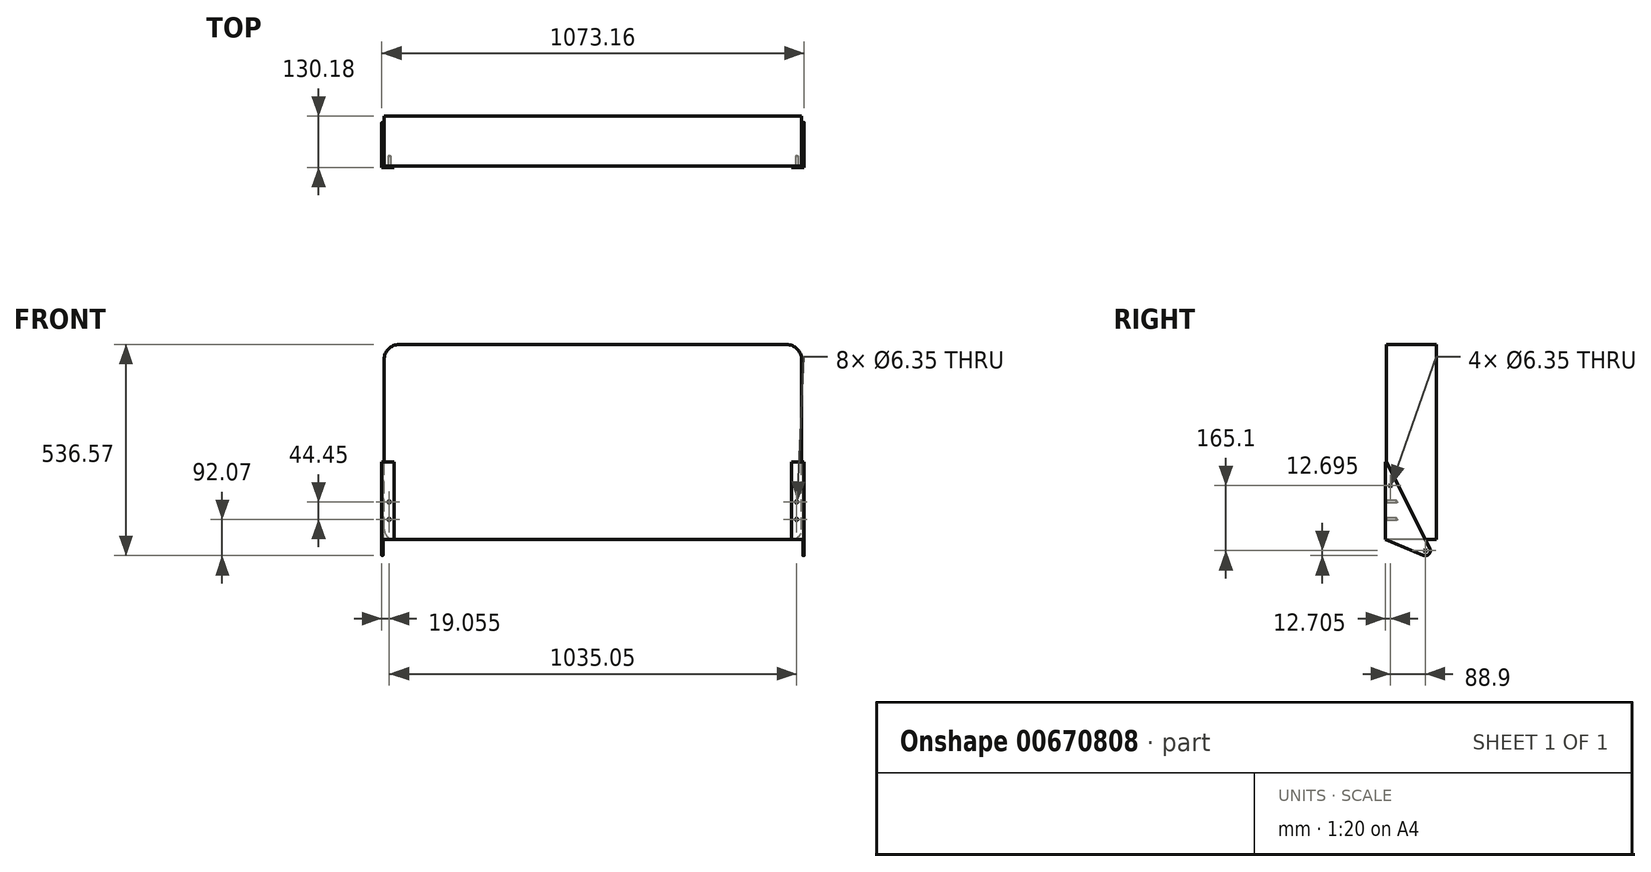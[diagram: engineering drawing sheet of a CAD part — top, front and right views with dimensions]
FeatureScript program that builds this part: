
annotation { "Feature Type Name" : "Feature", "Feature Type Description" : "" }
export const myFeature = defineFeature(function(context is Context, id is Id, definition is map)
    precondition{}
    {
        {
            var Q0;
            Q0=qCreatedBy(makeId("Front.planeOp"),FACE);
            var sketch = newSketch(context, id + "F0", { "sketchPlane" : qUnion([Q0])});
            skLineSegment(sketch, "E0.bottom", {"start": v(504.83, 0) * mm, "end": v(-504.83, 0) * mm});
            skLineSegment(sketch, "E0.top", {"start": v(492.13, 495.3) * mm, "end": v(-492.13, 495.3) * mm});
            skLineSegment(sketch, "E0.left", {"start": v(530.23, 25.4) * mm, "end": v(530.23, 457.2) * mm});
            skLineSegment(sketch, "E0.right", {"start": v(-530.23, 25.4) * mm, "end": v(-530.23, 457.2) * mm});
            skPoint(sketch, "E1.visualSharp", {"position": v(530.23, 495.3) * mm});
            skArc(sketch, "E1.filletArc", {"start": v(530.23, 457.2) * mm, "mid": v(519.07, 484.14) * mm, "end": v(492.13, 495.3) * mm});
            skPoint(sketch, "E2.visualSharp", {"position": v(-530.23, 495.3) * mm});
            skArc(sketch, "E2.filletArc", {"start": v(-492.13, 495.3) * mm, "mid": v(-519.07, 484.14) * mm, "end": v(-530.23, 457.2) * mm});
            skPoint(sketch, "E3.visualSharp", {"position": v(530.23, 0) * mm});
            skArc(sketch, "E3.filletArc", {"start": v(504.83, 0) * mm, "mid": v(522.79, 7.44) * mm, "end": v(530.23, 25.4) * mm});
            skPoint(sketch, "E4.visualSharp", {"position": v(-530.23, 0) * mm});
            skArc(sketch, "E4.filletArc", {"start": v(-530.22, 25.4) * mm, "mid": v(-522.79, 7.44) * mm, "end": v(-504.83, 0) * mm});
            skLineSegment(sketch, "E5", {"start": v(530.23, 241.3) * mm, "end": v(415.93, 241.3) * mm, "construction": true});
            skLineSegment(sketch, "E6", {"start": v(415.93, 241.3) * mm, "end": v(117.48, 241.3) * mm, "construction": true});
            skLineSegment(sketch, "E7", {"start": v(117.48, 241.3) * mm, "end": v(-104.77, 241.3) * mm, "construction": true});
            skLineSegment(sketch, "E8", {"start": v(-104.77, 241.3) * mm, "end": v(-403.22, 241.3) * mm, "construction": true});
            skLineSegment(sketch, "E9", {"start": v(-403.22, 241.3) * mm, "end": v(-530.23, 241.3) * mm, "construction": true});
            skLineSegment(sketch, "E10", {"start": v(415.93, 0) * mm, "end": v(415.93, 495.3) * mm});
            skLineSegment(sketch, "E11", {"start": v(117.48, 0) * mm, "end": v(117.48, 495.3) * mm});
            skLineSegment(sketch, "E12", {"start": v(-104.77, 0) * mm, "end": v(-104.77, 495.3) * mm});
            skLineSegment(sketch, "E13", {"start": v(-403.22, 0) * mm, "end": v(-403.22, 495.3) * mm});
            skLineSegment(sketch, "E14", {"start": v(-517.52, 0) * mm, "end": v(-517.52, 50.8) * mm, "construction": true});
            skLineSegment(sketch, "E15", {"start": v(-517.52, 50.8) * mm, "end": v(-530.22, 50.8) * mm, "construction": true});
            skLineSegment(sketch, "E16", {"start": v(-517.52, 50.8) * mm, "end": v(-517.52, 95.25) * mm, "construction": true});
            skLineSegment(sketch, "E17.MirrorCS", {"start": v(517.52, 50.8) * mm, "end": v(517.52, 95.25) * mm, "construction": true});
            skLineSegment(sketch, "E18.MirrorCS", {"start": v(517.52, 50.8) * mm, "end": v(530.22, 50.8) * mm, "construction": true});
            skLineSegment(sketch, "E19.MirrorCS", {"start": v(517.52, 0) * mm, "end": v(517.52, 50.8) * mm, "construction": true});
            skSolve(sketch);
        }
        {
            var Q0;
            Q0=makeQuery(id+"F0.imprint","IMPRINT",FACE,{"disambiguationData":[TD([[makeQuery(id+"F0.imprint","IMPRINT",EDGE,{"derivedFrom":sQuery(id+"F0.wireOp",EDGE,"E0.left")}),1.0]])]});
            var Q1;
            {var subQ0=sQuery(id+"F0.wireOp",EDGE,"E10");Q1=makeQuery(id+"F0.imprint","IMPRINT",FACE,{"disambiguationData":[TD([[makeQuery(id+"F0.imprint","IMPRINT",EDGE,{"derivedFrom":subQ0}),1.0]])]});}
            var Q2;
            {var subQ0=sQuery(id+"F0.wireOp",EDGE,"E11");Q2=makeQuery(id+"F0.imprint","IMPRINT",FACE,{"disambiguationData":[TD([[makeQuery(id+"F0.imprint","IMPRINT",EDGE,{"derivedFrom":subQ0}),1.0]])]});}
            var Q3;
            {var subQ0=sQuery(id+"F0.wireOp",EDGE,"E12");Q3=makeQuery(id+"F0.imprint","IMPRINT",FACE,{"disambiguationData":[TD([[makeQuery(id+"F0.imprint","IMPRINT",EDGE,{"derivedFrom":subQ0}),1.0]])]});}
            var Q4;
            Q4=makeQuery(id+"F0.imprint","IMPRINT",FACE,{"disambiguationData":[TD([[makeQuery(id+"F0.imprint","IMPRINT",EDGE,{"derivedFrom":sQuery(id+"F0.wireOp",EDGE,"E0.right")}),-1.0]])]});
            extrude(context, id + "F1", {"entities" : qUnion([Q0, Q1, Q2, Q3, Q4]), "oppositeDirection" : true, "depth" : 127 * mm, "offsetDistance" : 25.4 * mm});
        }
        {
            var Q0;
            Q0=sQuery(id+"F0.wireOp",VERTEX,"E16.end");
            var Q1;
            Q1=sQuery(id+"F0.wireOp",VERTEX,"E16.start");
            var Q2;
            Q2=sQuery(id+"F0.wireOp",VERTEX,"E17.MirrorCS.end");
            var Q3;
            Q3=sQuery(id+"F0.wireOp",VERTEX,"E19.MirrorCS.end");
            var Q4;
            Q4=makeQuery(id+"F1.opExtrude","SWEPT_BODY",BODY,{"disambiguationData":[OSD([sQuery(id+"F0.wireOp",EDGE,"E0.bottom"),sQuery(id+"F0.wireOp",EDGE,"E0.top"),sQuery(id+"F0.wireOp",EDGE,"E0.left"),sQuery(id+"F0.wireOp",EDGE,"E0.right"),sQuery(id+"F0.wireOp",EDGE,"E1.filletArc"),sQuery(id+"F0.wireOp",EDGE,"E2.filletArc"),sQuery(id+"F0.wireOp",EDGE,"E3.filletArc"),sQuery(id+"F0.wireOp",EDGE,"E4.filletArc")])]});
            hole(context, id + "F2", {"style" : HoleStyle.SIMPLE, "endStyle" : HoleEndStyle.BLIND, "holeDiameter" : 6.35 * mm, "majorDiameter" : 6.35 * mm, "holeDepth" : 25.4 * mm, "isTappedThrough" : true, "tappedDepth" : 12.7 * mm, "tapClearance" : 3, "locations" : qUnion([Q0, Q1, Q2, Q3]), "scope" : qUnion([Q4])});
        }
        {
            var Q0;
            Q0=makeQuery(id+"F0.imprint","IMPRINT",FACE,{"disambiguationData":[TD([[makeQuery(id+"F0.imprint","IMPRINT",EDGE,{"derivedFrom":sQuery(id+"F0.wireOp",EDGE,"E0.left")}),1.0]])]});
            var sketch = newSketch(context, id + "F3", { "sketchPlane" : qUnion([Q0])});
            skLineSegment(sketch, "E20.0", {"start": v(517.52, 50.8) * mm, "end": v(517.52, 95.25) * mm, "construction": true});
            skLineSegment(sketch, "E20.1", {"start": v(517.52, 0) * mm, "end": v(517.52, 50.8) * mm, "construction": true});
            skLineSegment(sketch, "E21.0", {"start": v(498.48, 0) * mm, "end": v(-504.83, 0) * mm, "construction": true});
            skLineSegment(sketch, "E22.0", {"start": v(530.23, 25.4) * mm, "end": v(530.23, 457.2) * mm, "construction": true});
            skLineSegment(sketch, "E23.bottom", {"start": v(504.82, 196.85) * mm, "end": v(536.58, 196.85) * mm});
            skLineSegment(sketch, "E23.top", {"start": v(504.82, 0) * mm, "end": v(536.58, 0) * mm});
            skLineSegment(sketch, "E23.left", {"start": v(504.82, 196.85) * mm, "end": v(504.82, 0) * mm});
            skLineSegment(sketch, "E23.right", {"start": v(536.58, 196.85) * mm, "end": v(536.58, 0) * mm});
            skLineSegment(sketch, "E24", {"start": v(517.52, 95.25) * mm, "end": v(517.52, 196.85) * mm, "construction": true});
            skLineSegment(sketch, "E25", {"start": v(517.52, 95.25) * mm, "end": v(504.82, 95.25) * mm, "construction": true});
            skLineSegment(sketch, "E26", {"start": v(530.23, 95.25) * mm, "end": v(536.58, 95.25) * mm, "construction": true});
            skArc(sketch, "E27.0", {"start": v(504.83, 0) * mm, "mid": v(522.79, 7.44) * mm, "end": v(530.23, 25.4) * mm, "construction": true});
            skSolve(sketch);
        }
        {
            var Q0;
            {var subQ0=sQuery(id+"F3.wireOp",EDGE,"E23.left");Q0=makeQuery(id+"F3.imprint","IMPRINT",FACE,{"disambiguationData":[TD([[makeQuery(id+"F3.imprint","IMPRINT",EDGE,{"derivedFrom":subQ0}),1.0]])]});}
            var Q1;
            Q1=makeQuery(id+"F3.imprint","IMPRINT",FACE,{"disambiguationData":[TD([[makeQuery(id+"F3.imprint","IMPRINT",EDGE,{"derivedFrom":sQuery(id+"F3.wireOp",EDGE,"E23.top")}),1.0]])]});
            extrude(context, id + "F4", {"entities" : qUnion([Q0, Q1]), "depth" : 3.17 * mm, "offsetDistance" : 25.4 * mm});
        }
        {
            var Q0;
            Q0=sQuery(id+"F0.wireOp",VERTEX,"E17.MirrorCS.end");
            var Q1;
            Q1=sQuery(id+"F0.wireOp",VERTEX,"E17.MirrorCS.start");
            var Q2;
            Q2=makeQuery(id+"F4.opExtrude","SWEPT_BODY",BODY,{"disambiguationData":[OSD([sQuery(id+"F3.wireOp",EDGE,"E23.bottom"),sQuery(id+"F3.wireOp",EDGE,"E23.top"),sQuery(id+"F3.wireOp",EDGE,"E23.left"),sQuery(id+"F3.wireOp",EDGE,"E23.right")])]});
            hole(context, id + "F5", {"style" : HoleStyle.SIMPLE, "endStyle" : HoleEndStyle.THROUGH, "oppositeDirection" : true, "holeDiameter" : 6.35 * mm, "majorDiameter" : 6.35 * mm, "isTappedThrough" : true, "tappedDepth" : 12.7 * mm, "tapClearance" : 3, "locations" : qUnion([Q0, Q1]), "scope" : qUnion([Q2])});
        }
        {
            var Q0;
            Q0=makeQuery(id+"F4.opExtrude","SWEPT_FACE",FACE,{"disambiguationData":[OSD([sQuery(id+"F3.wireOp",EDGE,"E23.right")])]});
            var sketch = newSketch(context, id + "F6", { "sketchPlane" : qUnion([Q0])});
            skLineSegment(sketch, "E28.0", {"start": v(0, 50.8) * mm, "end": v(0, 95.25) * mm, "construction": true});
            skLineSegment(sketch, "E29", {"start": v(0, 50.8) * mm, "end": v(0, -28.58) * mm, "construction": true});
            skLineSegment(sketch, "E30", {"start": v(0, -28.58) * mm, "end": v(98.43, -28.58) * mm, "construction": true});
            skArc(sketch, "E31", {"start": v(93.54, -40.3) * mm, "mid": v(107.7, -37.24) * mm, "end": v(109.79, -22.9) * mm});
            skLineSegment(sketch, "E32", {"start": v(0, 196.85) * mm, "end": v(109.79, -22.9) * mm});
            skLineSegment(sketch, "E33.0", {"start": v(-3.18, 196.85) * mm, "end": v(-3.18, 0) * mm});
            skLineSegment(sketch, "E34.0", {"start": v(-3.18, 196.85) * mm, "end": v(0, 196.85) * mm});
            skLineSegment(sketch, "E35", {"start": v(-3.17, 0) * mm, "end": v(93.54, -40.3) * mm});
            skLineSegment(sketch, "E36", {"start": v(98.43, -28.58) * mm, "end": v(98.43, 136.52) * mm, "construction": true});
            skLineSegment(sketch, "E37", {"start": v(98.43, 136.52) * mm, "end": v(9.53, 136.52) * mm, "construction": true});
            skSolve(sketch);
        }
        {
            var Q0;
            Q0=makeQuery(id+"F6.imprint","IMPRINT",FACE,{"disambiguationData":[TD([[makeQuery(id+"F6.imprint","IMPRINT",EDGE,{"derivedFrom":sQuery(id+"F6.wireOp",EDGE,"E31")}),1.0]])]});
            var Q1;
            Q1=makeQuery(id+"F6.imprint","IMPRINT",FACE,{"disambiguationData":[TD([[makeQuery(id+"F6.imprint","IMPRINT",EDGE,{"derivedFrom":sQuery(id+"F6.wireOp",EDGE,"E33.0")}),1.0]])]});
            extrude(context, id + "F7", {"entities" : qUnion([Q0, Q1]), "operationType" : NewBodyOperationType.ADD, "oppositeDirection" : true, "depth" : 3.17 * mm, "offsetDistance" : 25.4 * mm});
        }
        {
            var Q0;
            Q0=sQuery(id+"F6.wireOp",VERTEX,"E30.end");
            var Q1;
            Q1=sQuery(id+"F6.wireOp",VERTEX,"E37.end");
            var Q2;
            Q2=makeQuery(id+"F4.opExtrude","SWEPT_BODY",BODY,{"disambiguationData":[OSD([sQuery(id+"F3.wireOp",EDGE,"E23.bottom"),sQuery(id+"F3.wireOp",EDGE,"E23.top"),sQuery(id+"F3.wireOp",EDGE,"E23.left"),sQuery(id+"F3.wireOp",EDGE,"E23.right")])]});
            hole(context, id + "F8", {"style" : HoleStyle.SIMPLE, "endStyle" : HoleEndStyle.THROUGH, "holeDiameter" : 6.35 * mm, "majorDiameter" : 6.35 * mm, "isTappedThrough" : true, "tappedDepth" : 12.7 * mm, "tapClearance" : 3, "locations" : qUnion([Q0, Q1]), "scope" : qUnion([Q2])});
        }
        {
            var Q0;
            Q0=makeQuery(id+"F4.opExtrude","SWEPT_BODY",BODY,{"disambiguationData":[OSD([sQuery(id+"F3.wireOp",EDGE,"E23.bottom"),sQuery(id+"F3.wireOp",EDGE,"E23.top"),sQuery(id+"F3.wireOp",EDGE,"E23.left"),sQuery(id+"F3.wireOp",EDGE,"E23.right")])]});
            var Q1;
            Q1=qCreatedBy(makeId("Right.planeOp"),FACE);
            mirror(context, id + "F9", {"entities" : qUnion([Q0]), "mirrorPlane" : qUnion([Q1])});
        }
    });
